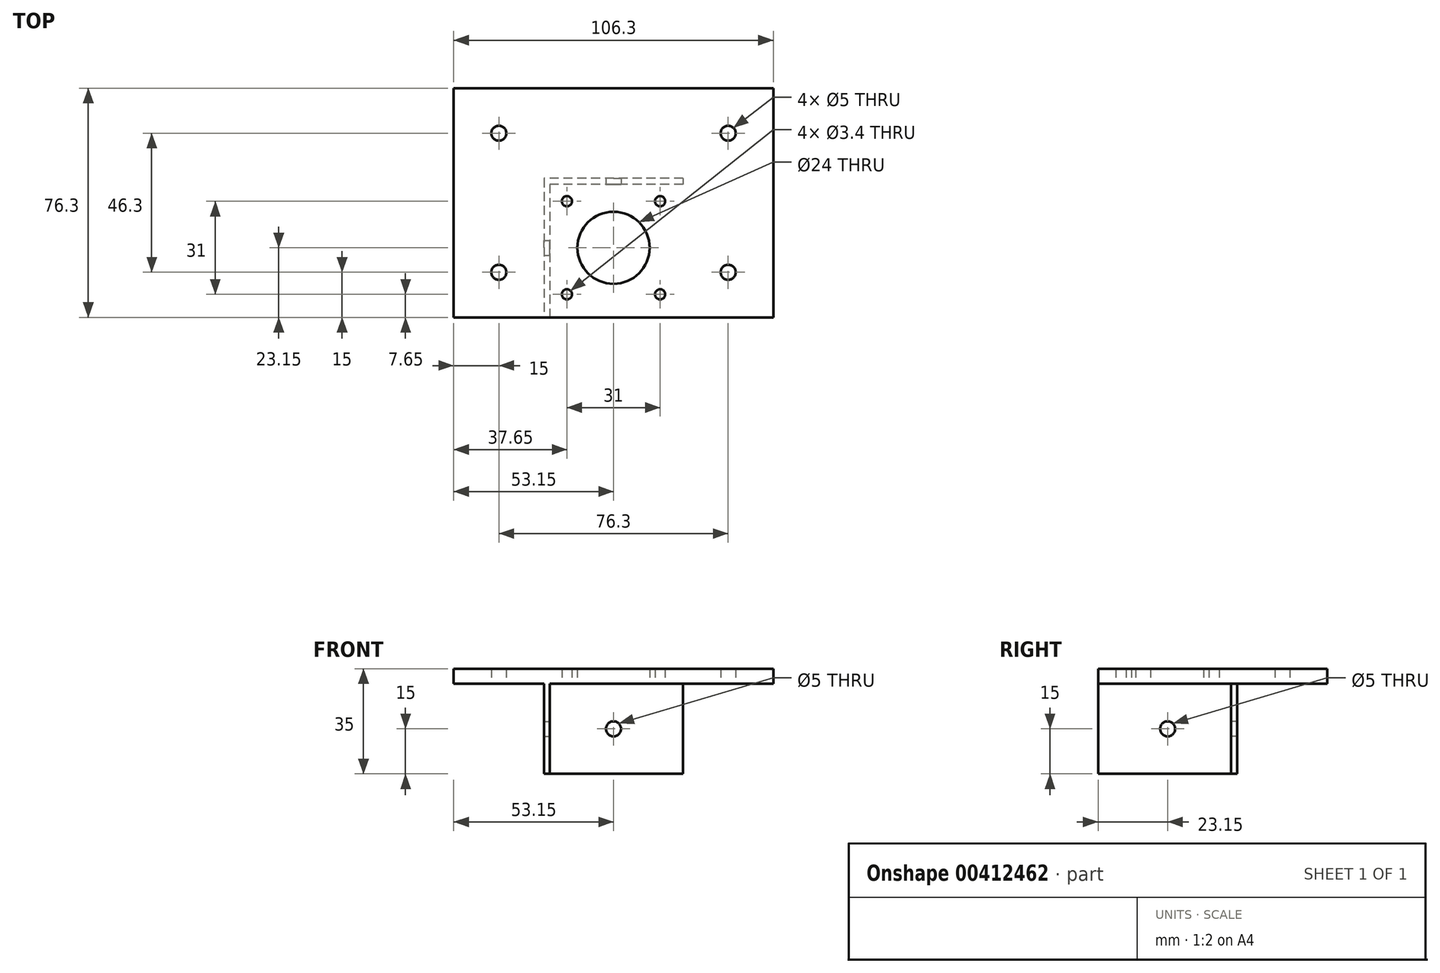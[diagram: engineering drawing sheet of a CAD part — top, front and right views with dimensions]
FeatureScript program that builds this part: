
annotation { "Feature Type Name" : "Feature", "Feature Type Description" : "" }
export const myFeature = defineFeature(function(context is Context, id is Id, definition is map)
    precondition{}
    {
        {
            var Q0;
            Q0=qCreatedBy(makeId("Top.planeOp"),FACE);
            var sketch = newSketch(context, id + "F0", { "sketchPlane" : qUnion([Q0])});
            skLineSegment(sketch, "E0.bottom", {"start": v(21.15, 21.15) * mm, "end": v(-21.15, 21.15) * mm});
            skLineSegment(sketch, "E0.top", {"start": v(21.15, -21.15) * mm, "end": v(-21.15, -21.15) * mm});
            skLineSegment(sketch, "E0.left", {"start": v(21.15, 21.15) * mm, "end": v(21.15, -21.15) * mm});
            skLineSegment(sketch, "E0.right", {"start": v(-21.15, 21.15) * mm, "end": v(-21.15, -21.15) * mm});
            skPoint(sketch, "E0.middle", {"position": v(0, 0) * mm});
            skLineSegment(sketch, "E1.bottom", {"start": v(15.5, 15.5) * mm, "end": v(-15.5, 15.5) * mm});
            skLineSegment(sketch, "E1.top", {"start": v(15.5, -15.5) * mm, "end": v(-15.5, -15.5) * mm});
            skLineSegment(sketch, "E1.left", {"start": v(15.5, 15.5) * mm, "end": v(15.5, -15.5) * mm});
            skLineSegment(sketch, "E1.right", {"start": v(-15.5, 15.5) * mm, "end": v(-15.5, -15.5) * mm});
            skCircle(sketch, "E2", {"center": v(-15.5, 15.5) * mm, "radius": 1.5 * mm});
            skCircle(sketch, "E3", {"center": v(15.5, 15.5) * mm, "radius": 1.5 * mm});
            skCircle(sketch, "E4", {"center": v(15.5, -15.5) * mm, "radius": 1.5 * mm});
            skCircle(sketch, "E5", {"center": v(-15.5, -15.5) * mm, "radius": 1.5 * mm});
            skCircle(sketch, "E6", {"center": v(0, 0) * mm, "radius": 11 * mm});
            skCircle(sketch, "E7", {"center": v(0, 0) * mm, "radius": 2.5 * mm});
            skCircle(sketch, "E8.0", {"center": v(0, 0) * mm, "radius": 12 * mm});
            skLineSegment(sketch, "E9.0", {"start": v(23.15, 23.15) * mm, "end": v(-23.15, 23.15) * mm});
            skLineSegment(sketch, "E9.1", {"start": v(23.15, 23.15) * mm, "end": v(23.15, -23.15) * mm});
            skLineSegment(sketch, "E9.2", {"start": v(23.15, -23.15) * mm, "end": v(-23.15, -23.15) * mm});
            skLineSegment(sketch, "E9.3", {"start": v(-23.15, 23.15) * mm, "end": v(-23.15, -23.15) * mm});
            skCircle(sketch, "E10.0", {"center": v(-15.5, 15.5) * mm, "radius": 1.7 * mm});
            skCircle(sketch, "E11.0", {"center": v(15.5, 15.5) * mm, "radius": 1.7 * mm});
            skCircle(sketch, "E12.0", {"center": v(15.5, -15.5) * mm, "radius": 1.7 * mm});
            skCircle(sketch, "E13.0", {"center": v(-15.5, -15.5) * mm, "radius": 1.7 * mm});
            skLineSegment(sketch, "E14.0", {"start": v(-53.15, 53.15) * mm, "end": v(-53.15, -23.15) * mm});
            skLineSegment(sketch, "E14.1", {"start": v(53.15, 53.15) * mm, "end": v(-53.15, 53.15) * mm});
            skLineSegment(sketch, "E14.2", {"start": v(53.15, 53.15) * mm, "end": v(53.15, -23.15) * mm});
            skLineSegment(sketch, "E15", {"start": v(-53.15, -23.15) * mm, "end": v(-23.15, -23.15) * mm});
            skLineSegment(sketch, "E16", {"start": v(23.15, -23.15) * mm, "end": v(53.15, -23.15) * mm});
            skCircle(sketch, "E17", {"center": v(-38.15, 38.15) * mm, "radius": 2.5 * mm});
            skCircle(sketch, "E18", {"center": v(38.15, 38.15) * mm, "radius": 2.5 * mm});
            skCircle(sketch, "E19", {"center": v(-38.15, -8.15) * mm, "radius": 2.5 * mm});
            skCircle(sketch, "E20", {"center": v(38.15, -8.15) * mm, "radius": 2.5 * mm});
            skLineSegment(sketch, "E21", {"start": v(-21.15, 21.15) * mm, "end": v(-23.15, 21.15) * mm});
            skLineSegment(sketch, "E22", {"start": v(21.15, 21.15) * mm, "end": v(23.15, 21.15) * mm});
            skLineSegment(sketch, "E23", {"start": v(21.15, -21.15) * mm, "end": v(21.15, -23.15) * mm});
            skLineSegment(sketch, "E24", {"start": v(-21.15, -21.15) * mm, "end": v(-21.15, -23.15) * mm});
            skSolve(sketch);
        }
        {
            var Q0;
            Q0=makeQuery(id+"F0.imprint","IMPRINT",FACE,{"disambiguationData":[TD([[makeQuery(id+"F0.imprint","IMPRINT",EDGE,{"derivedFrom":sQuery(id+"F0.wireOp",EDGE,"E0.bottom")}),-1.0]])]});
            var Q1;
            Q1=makeQuery(id+"F0.imprint","IMPRINT",FACE,{"disambiguationData":[TD([[makeQuery(id+"F0.imprint","IMPRINT",EDGE,{"derivedFrom":sQuery(id+"F0.wireOp",EDGE,"E0.bottom")}),1.0]])]});
            var Q2;
            Q2=makeQuery(id+"F0.imprint","IMPRINT",FACE,{"disambiguationData":[TD([[makeQuery(id+"F0.imprint","IMPRINT",EDGE,{"derivedFrom":sQuery(id+"F0.wireOp",EDGE,"E8.0")}),-1.0]])]});
            var Q3;
            Q3=makeQuery(id+"F0.imprint","IMPRINT",FACE,{"disambiguationData":[TD([[makeQuery(id+"F0.imprint","IMPRINT",EDGE,{"derivedFrom":sQuery(id+"F0.wireOp",EDGE,"E9.0")}),-1.0]])]});
            var Q4;
            Q4=makeQuery(id+"F0.imprint","IMPRINT",FACE,{"disambiguationData":[TD([[makeQuery(id+"F0.imprint","IMPRINT",EDGE,{"derivedFrom":sQuery(id+"F0.wireOp",EDGE,"E0.right")}),-1.0]])]});
            var Q5;
            Q5=makeQuery(id+"F0.imprint","IMPRINT",FACE,{"disambiguationData":[TD([[makeQuery(id+"F0.imprint","IMPRINT",EDGE,{"derivedFrom":sQuery(id+"F0.wireOp",EDGE,"E0.left")}),1.0]])]});
            var Q6;
            Q6=makeQuery(id+"F0.imprint","IMPRINT",FACE,{"disambiguationData":[TD([[makeQuery(id+"F0.imprint","IMPRINT",EDGE,{"derivedFrom":sQuery(id+"F0.wireOp",EDGE,"E0.top")}),1.0]])]});
            extrude(context, id + "F1", {"entities" : qUnion([Q0, Q1, Q2, Q3, Q4, Q5, Q6]), "depth" : 5 * mm});
        }
        {
            var Q0;
            Q0=makeQuery(id+"F0.imprint","IMPRINT",FACE,{"disambiguationData":[TD([[makeQuery(id+"F0.imprint","IMPRINT",EDGE,{"derivedFrom":sQuery(id+"F0.wireOp",EDGE,"E0.bottom")}),-1.0]])]});
            var Q1;
            Q1=makeQuery(id+"F0.imprint","IMPRINT",FACE,{"disambiguationData":[TD([[makeQuery(id+"F0.imprint","IMPRINT",EDGE,{"derivedFrom":sQuery(id+"F0.wireOp",EDGE,"E0.right")}),-1.0]])]});
            extrude(context, id + "F2", {"entities" : qUnion([Q0, Q1]), "operationType" : NewBodyOperationType.ADD, "oppositeDirection" : true, "depth" : 30 * mm});
        }
        {
            var Q0;
            Q0=makeQuery(id+"F2.opExtrude","SWEPT_FACE",FACE,{"disambiguationData":[OSD([sQuery(id+"F0.wireOp",EDGE,"E0.right"),sQuery(id+"F0.wireOp",EDGE,"E24")])]});
            cPlane(context, id + "F3", {"entities" : qUnion([Q0]), "cplaneType" : CPlaneType.OFFSET, "offset" : 0 * mm, "width" : 150 * mm, "height" : 150 * mm});
        }
        {
            var Q0;
            Q0=qCreatedBy(id+"F3.planeOp",FACE);
            var sketch = newSketch(context, id + "F4", { "sketchPlane" : qUnion([Q0])});
            skPoint(sketch, "E25", {"position": v(0, -15) * mm});
            skSolve(sketch);
        }
        {
            var Q0;
            Q0=makeQuery(id+"F2.opExtrude","SWEPT_FACE",FACE,{"disambiguationData":[OSD([sQuery(id+"F0.wireOp",EDGE,"E0.bottom"),sQuery(id+"F0.wireOp",EDGE,"E22")])]});
            var sketch = newSketch(context, id + "F5", { "sketchPlane" : qUnion([Q0])});
            skPoint(sketch, "E26", {"position": v(0, -15) * mm});
            skSolve(sketch);
        }
        {
            var Q0;
            Q0=sQuery(id+"F4.wireOp",VERTEX,"E25");
            var Q1;
            Q1=sQuery(id+"F5.wireOp",VERTEX,"E26");
            var Q2;
            Q2=makeQuery(id+"F1.opExtrude","SWEPT_BODY",BODY,{"disambiguationData":[OSD([sQuery(id+"F0.wireOp",EDGE,"E8.0"),sQuery(id+"F0.wireOp",EDGE,"E9.2"),sQuery(id+"F0.wireOp",EDGE,"E10.0"),sQuery(id+"F0.wireOp",EDGE,"E11.0"),sQuery(id+"F0.wireOp",EDGE,"E12.0"),sQuery(id+"F0.wireOp",EDGE,"E13.0"),sQuery(id+"F0.wireOp",EDGE,"E14.0"),sQuery(id+"F0.wireOp",EDGE,"E14.1"),sQuery(id+"F0.wireOp",EDGE,"E14.2"),sQuery(id+"F0.wireOp",EDGE,"E15"),sQuery(id+"F0.wireOp",EDGE,"E16"),sQuery(id+"F0.wireOp",EDGE,"E17"),sQuery(id+"F0.wireOp",EDGE,"E18"),sQuery(id+"F0.wireOp",EDGE,"E19"),sQuery(id+"F0.wireOp",EDGE,"E20")])]});
            hole(context, id + "F6", {"style" : HoleStyle.SIMPLE, "endStyle" : HoleEndStyle.BLIND, "holeDiameter" : 5 * mm, "holeDepth" : 12.7 * mm, "isTappedThrough" : true, "tappedDepth" : 12 * mm, "tapClearance" : 3, "locations" : qUnion([Q0, Q1]), "scope" : qUnion([Q2])});
        }
    });
